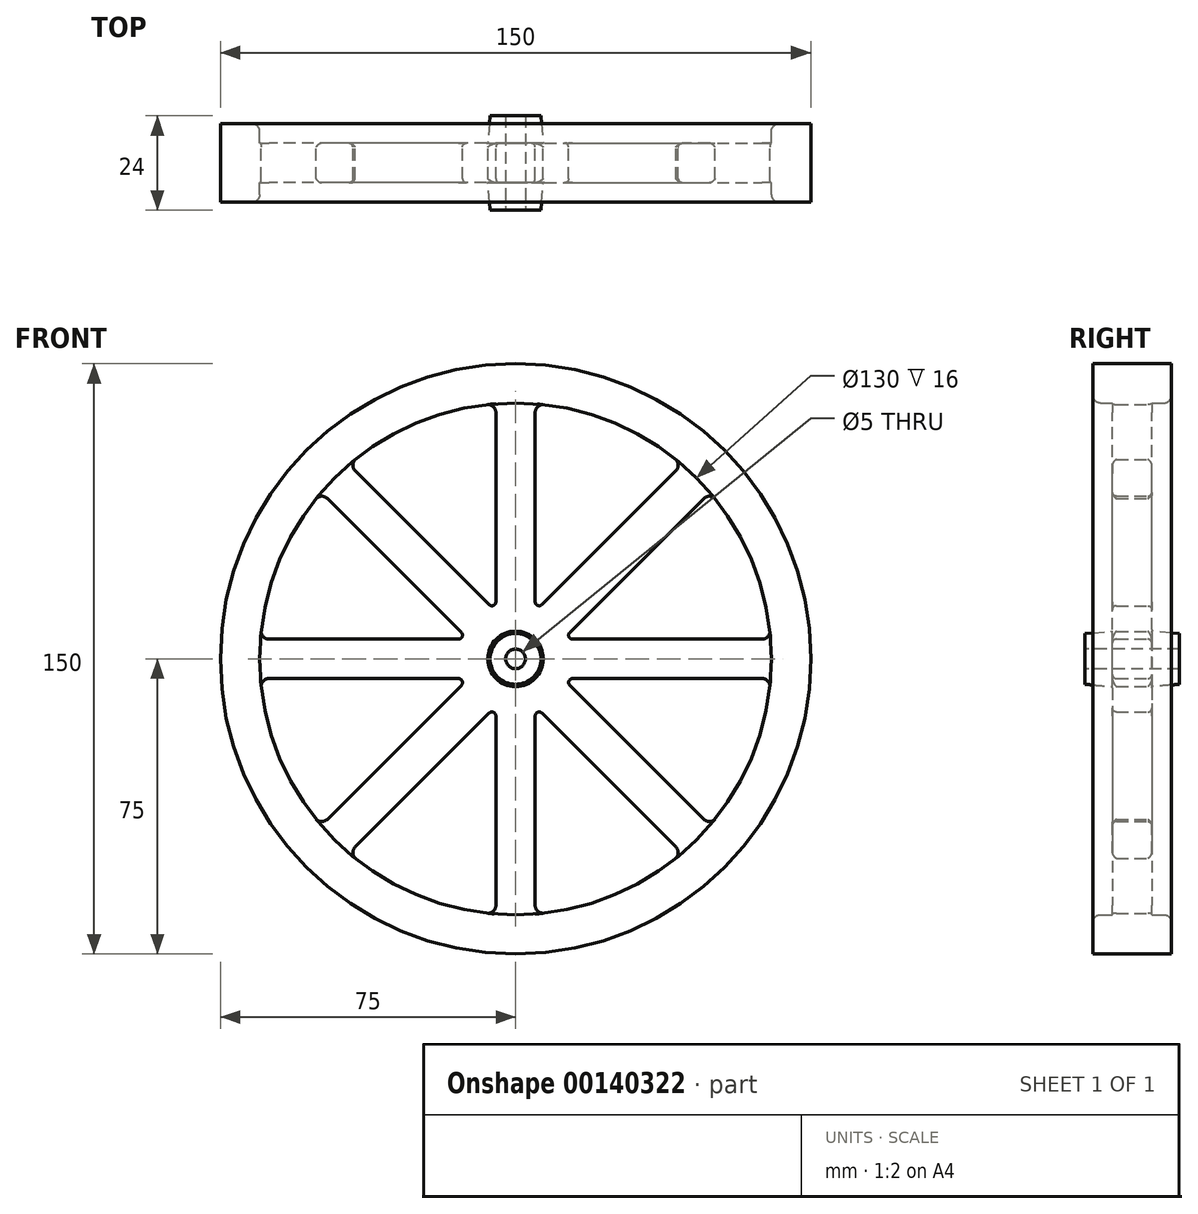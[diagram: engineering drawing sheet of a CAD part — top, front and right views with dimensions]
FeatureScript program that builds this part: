
annotation { "Feature Type Name" : "Feature", "Feature Type Description" : "" }
export const myFeature = defineFeature(function(context is Context, id is Id, definition is map)
    precondition{}
    {
        {
            var Q0;
            Q0=qCreatedBy(makeId("Front.planeOp"),FACE);
            var sketch = newSketch(context, id + "F0", { "sketchPlane" : qUnion([Q0])});
            skCircle(sketch, "E0", {"center": v(0, 0) * mm, "radius": 75 * mm});
            skLineSegment(sketch, "E1", {"start": v(0, 0) * mm, "end": v(-53.03, 53.03) * mm, "construction": true});
            skLineSegment(sketch, "E2", {"start": v(-6.7, 13.78) * mm, "end": v(-40.74, 47.82) * mm});
            skLineSegment(sketch, "E3", {"start": v(-5, 14.49) * mm, "end": v(-5, 62.62) * mm});
            skLineSegment(sketch, "E4", {"start": v(0, 0) * mm, "end": v(-5, 12.07) * mm, "construction": true});
            skCircle(sketch, "E5.1.7.0", {"center": v(0, 0) * mm, "radius": 65 * mm});
            skPoint(sketch, "E6.visualSharp", {"position": v(-14.87, 21.95) * mm});
            skArc(sketch, "E6.filletArc", {"start": v(-40.74, 50.64) * mm, "mid": v(-41.33, 49.23) * mm, "end": v(-40.74, 47.82) * mm});
            skPoint(sketch, "E7.visualSharp", {"position": v(-5, 26.04) * mm});
            skArc(sketch, "E7.filletArc", {"start": v(-5, 62.62) * mm, "mid": v(-5.59, 64.04) * mm, "end": v(-7, 64.62) * mm});
            skPoint(sketch, "E8.visualSharp", {"position": v(-5, 12.07) * mm});
            skArc(sketch, "E8.filletArc", {"start": v(-6.7, 13.78) * mm, "mid": v(-5.62, 13.56) * mm, "end": v(-5, 14.49) * mm});
            skArc(sketch, "E9.1.0", {"start": v(-64.62, 7) * mm, "mid": v(-64.04, 5.59) * mm, "end": v(-62.62, 5) * mm});
            skLineSegment(sketch, "E9.1.1", {"start": v(-14.49, 5) * mm, "end": v(-62.62, 5) * mm});
            skArc(sketch, "E9.1.2", {"start": v(-14.49, 5) * mm, "mid": v(-13.56, 5.62) * mm, "end": v(-13.78, 6.7) * mm});
            skLineSegment(sketch, "E9.1.3", {"start": v(-13.78, 6.7) * mm, "end": v(-47.82, 40.74) * mm});
            skArc(sketch, "E9.1.4", {"start": v(-47.82, 40.74) * mm, "mid": v(-49.23, 41.33) * mm, "end": v(-50.64, 40.74) * mm});
            skArc(sketch, "E9.2.0", {"start": v(-50.64, -40.74) * mm, "mid": v(-49.23, -41.33) * mm, "end": v(-47.82, -40.74) * mm});
            skLineSegment(sketch, "E9.2.1", {"start": v(-13.78, -6.7) * mm, "end": v(-47.82, -40.74) * mm});
            skArc(sketch, "E9.2.2", {"start": v(-13.78, -6.7) * mm, "mid": v(-13.56, -5.62) * mm, "end": v(-14.49, -5) * mm});
            skLineSegment(sketch, "E9.2.3", {"start": v(-14.49, -5) * mm, "end": v(-62.62, -5) * mm});
            skArc(sketch, "E9.2.4", {"start": v(-62.62, -5) * mm, "mid": v(-64.04, -5.59) * mm, "end": v(-64.62, -7) * mm});
            skArc(sketch, "E9.3.0", {"start": v(-7, -64.62) * mm, "mid": v(-5.59, -64.04) * mm, "end": v(-5, -62.62) * mm});
            skLineSegment(sketch, "E9.3.1", {"start": v(-5, -14.49) * mm, "end": v(-5, -62.62) * mm});
            skArc(sketch, "E9.3.2", {"start": v(-5, -14.49) * mm, "mid": v(-5.62, -13.56) * mm, "end": v(-6.7, -13.78) * mm});
            skLineSegment(sketch, "E9.3.3", {"start": v(-6.7, -13.78) * mm, "end": v(-40.74, -47.82) * mm});
            skArc(sketch, "E9.3.4", {"start": v(-40.74, -47.82) * mm, "mid": v(-41.33, -49.23) * mm, "end": v(-40.74, -50.64) * mm});
            skArc(sketch, "E9.4.0", {"start": v(40.74, -50.64) * mm, "mid": v(41.33, -49.23) * mm, "end": v(40.74, -47.82) * mm});
            skLineSegment(sketch, "E9.4.1", {"start": v(6.7, -13.78) * mm, "end": v(40.74, -47.82) * mm});
            skArc(sketch, "E9.4.2", {"start": v(6.7, -13.78) * mm, "mid": v(5.62, -13.56) * mm, "end": v(5, -14.49) * mm});
            skLineSegment(sketch, "E9.4.3", {"start": v(5, -14.49) * mm, "end": v(5, -62.62) * mm});
            skArc(sketch, "E9.4.4", {"start": v(5, -62.62) * mm, "mid": v(5.59, -64.04) * mm, "end": v(7, -64.62) * mm});
            skArc(sketch, "E9.5.0", {"start": v(64.62, -7) * mm, "mid": v(64.04, -5.59) * mm, "end": v(62.62, -5) * mm});
            skLineSegment(sketch, "E9.5.1", {"start": v(14.49, -5) * mm, "end": v(62.62, -5) * mm});
            skArc(sketch, "E9.5.2", {"start": v(14.49, -5) * mm, "mid": v(13.56, -5.62) * mm, "end": v(13.78, -6.7) * mm});
            skLineSegment(sketch, "E9.5.3", {"start": v(13.78, -6.7) * mm, "end": v(47.82, -40.74) * mm});
            skArc(sketch, "E9.5.4", {"start": v(47.82, -40.74) * mm, "mid": v(49.23, -41.33) * mm, "end": v(50.64, -40.74) * mm});
            skArc(sketch, "E9.6.0", {"start": v(50.64, 40.74) * mm, "mid": v(49.23, 41.33) * mm, "end": v(47.82, 40.74) * mm});
            skLineSegment(sketch, "E9.6.1", {"start": v(13.78, 6.7) * mm, "end": v(47.82, 40.74) * mm});
            skArc(sketch, "E9.6.2", {"start": v(13.78, 6.7) * mm, "mid": v(13.56, 5.62) * mm, "end": v(14.49, 5) * mm});
            skLineSegment(sketch, "E9.6.3", {"start": v(14.49, 5) * mm, "end": v(62.62, 5) * mm});
            skArc(sketch, "E9.6.4", {"start": v(62.62, 5) * mm, "mid": v(64.04, 5.59) * mm, "end": v(64.62, 7) * mm});
            skArc(sketch, "E9.7.0", {"start": v(7, 64.62) * mm, "mid": v(5.59, 64.04) * mm, "end": v(5, 62.62) * mm});
            skLineSegment(sketch, "E9.7.1", {"start": v(5, 14.49) * mm, "end": v(5, 62.62) * mm});
            skArc(sketch, "E9.7.2", {"start": v(5, 14.49) * mm, "mid": v(5.62, 13.56) * mm, "end": v(6.7, 13.78) * mm});
            skLineSegment(sketch, "E9.7.3", {"start": v(6.7, 13.78) * mm, "end": v(40.74, 47.82) * mm});
            skArc(sketch, "E9.7.4", {"start": v(40.74, 47.82) * mm, "mid": v(41.33, 49.23) * mm, "end": v(40.74, 50.64) * mm});
            skCircle(sketch, "E10", {"center": v(0, 0) * mm, "radius": 2.5 * mm});
            skCircle(sketch, "E11", {"center": v(0, 0) * mm, "radius": 7.5 * mm});
            skLineSegment(sketch, "E12", {"start": v(6.7, 13.78) * mm, "end": v(5, 12.07) * mm, "construction": true});
            skLineSegment(sketch, "E13", {"start": v(5, 14.49) * mm, "end": v(5, 12.07) * mm, "construction": true});
            skSolve(sketch);
        }
        {
            var Q0;
            Q0=makeQuery(id+"F0.imprint","IMPRINT",FACE,{"disambiguationData":[TD([[makeQuery(id+"F0.imprint","IMPRINT",EDGE,{"derivedFrom":sQuery(id+"F0.wireOp",EDGE,"E0")}),1.0]])]});
            extrude(context, id + "F1", {"entities" : qUnion([Q0]), "endBound" : BoundingType.SYMMETRIC, "depth" : 20 * mm});
        }
        {
            var Q0;
            Q0=makeQuery(id+"F0.imprint","IMPRINT",FACE,{"disambiguationData":[TD([[makeQuery(id+"F0.imprint","IMPRINT",EDGE,{"derivedFrom":sQuery(id+"F0.wireOp",EDGE,"E2")}),1.0]])]});
            var Q1;
            Q1=makeQuery(id+"F0.imprint","IMPRINT",FACE,{"disambiguationData":[TD([[makeQuery(id+"F0.imprint","IMPRINT",EDGE,{"derivedFrom":sQuery(id+"F0.wireOp",EDGE,"E10")}),-1.0]])]});
            extrude(context, id + "F2", {"entities" : qUnion([Q0, Q1]), "operationType" : NewBodyOperationType.ADD, "endBound" : BoundingType.SYMMETRIC, "depth" : 10 * mm});
        }
        {
            var Q0;
            Q0=makeQuery(id+"F0.imprint","IMPRINT",FACE,{"disambiguationData":[TD([[makeQuery(id+"F0.imprint","IMPRINT",EDGE,{"derivedFrom":sQuery(id+"F0.wireOp",EDGE,"E10")}),-1.0]])]});
            var Q1;
            Q1=makeQuery(id+"F0.imprint","IMPRINT",FACE,{"disambiguationData":[TD([[makeQuery(id+"F0.imprint","IMPRINT",EDGE,{"derivedFrom":sQuery(id+"F0.wireOp",EDGE,"E10")}),1.0]])]});
            extrude(context, id + "F3", {"entities" : qUnion([Q0, Q1]), "operationType" : NewBodyOperationType.ADD, "endBound" : BoundingType.SYMMETRIC, "depth" : 24 * mm, "hasDraft" : true, "draftAngle" : 5 * degree, "draftPullDirection" : true});
        }
        {
            var Q0;
            Q0=makeQuery(id+"F0.imprint","IMPRINT",FACE,{"disambiguationData":[TD([[makeQuery(id+"F0.imprint","IMPRINT",EDGE,{"derivedFrom":sQuery(id+"F0.wireOp",EDGE,"E10")}),1.0]])]});
            extrude(context, id + "F4", {"entities" : qUnion([Q0]), "operationType" : NewBodyOperationType.REMOVE, "endBound" : BoundingType.SYMMETRIC, "oppositeDirection" : true, "depth" : 25 * mm});
        }
        {
            var Q0;
            Q0=makeQuery(id+"F1.opExtrude","CAP_EDGE",EDGE,{"disambiguationData":[OSD([sQuery(id+"F0.wireOp",EDGE,"E5.1.7.0")])],"isStart":true});
            var Q1;
            Q1=makeQuery(id+"F1.opExtrude","CAP_EDGE",EDGE,{"disambiguationData":[OSD([sQuery(id+"F0.wireOp",EDGE,"E5.1.7.0")])],"isStart":false});
            fillet(context, id + "F5", {"entities" : qUnion([Q0, Q1]), "radius" : 2 * mm, "tangentPropagation" : true, "allowEdgeOverflow" : false});
        }
        {
            var Q0;
            Q0=makeQuery(id+"F2.opExtrude","CAP_EDGE",EDGE,{"disambiguationData":[OSD([sQuery(id+"F0.wireOp",EDGE,"E9.1.3")])],"isStart":false});
            var Q1;
            Q1=makeQuery(id+"F2.opExtrude","CAP_EDGE",EDGE,{"disambiguationData":[OSD([sQuery(id+"F0.wireOp",EDGE,"E9.2.3")])],"isStart":false});
            var Q2;
            Q2=makeQuery(id+"F2.opExtrude","CAP_EDGE",EDGE,{"disambiguationData":[OSD([sQuery(id+"F0.wireOp",EDGE,"E9.3.3")])],"isStart":false});
            var Q3;
            Q3=makeQuery(id+"F2.opExtrude","CAP_EDGE",EDGE,{"disambiguationData":[OSD([sQuery(id+"F0.wireOp",EDGE,"E9.4.3")])],"isStart":false});
            var Q4;
            Q4=makeQuery(id+"F2.opExtrude","CAP_EDGE",EDGE,{"disambiguationData":[OSD([sQuery(id+"F0.wireOp",EDGE,"E9.5.3")])],"isStart":false});
            var Q5;
            Q5=makeQuery(id+"F2.opExtrude","CAP_EDGE",EDGE,{"disambiguationData":[OSD([sQuery(id+"F0.wireOp",EDGE,"E9.6.3")])],"isStart":false});
            var Q6;
            Q6=makeQuery(id+"F2.opExtrude","CAP_EDGE",EDGE,{"disambiguationData":[OSD([sQuery(id+"F0.wireOp",EDGE,"E9.7.3")])],"isStart":false});
            var Q7;
            Q7=makeQuery(id+"F2.opExtrude","CAP_EDGE",EDGE,{"disambiguationData":[OSD([sQuery(id+"F0.wireOp",EDGE,"E3")])],"isStart":false});
            var Q8;
            Q8=makeQuery(id+"F2.opExtrude","CAP_EDGE",EDGE,{"disambiguationData":[OSD([sQuery(id+"F0.wireOp",EDGE,"E9.2.3")])],"isStart":true});
            var Q9;
            Q9=makeQuery(id+"F2.opExtrude","CAP_EDGE",EDGE,{"disambiguationData":[OSD([sQuery(id+"F0.wireOp",EDGE,"E9.3.3")])],"isStart":true});
            var Q10;
            Q10=makeQuery(id+"F2.opExtrude","CAP_EDGE",EDGE,{"disambiguationData":[OSD([sQuery(id+"F0.wireOp",EDGE,"E3")])],"isStart":true});
            var Q11;
            Q11=makeQuery(id+"F2.opExtrude","CAP_EDGE",EDGE,{"disambiguationData":[OSD([sQuery(id+"F0.wireOp",EDGE,"E9.7.3")])],"isStart":true});
            var Q12;
            Q12=makeQuery(id+"F2.opExtrude","CAP_EDGE",EDGE,{"disambiguationData":[OSD([sQuery(id+"F0.wireOp",EDGE,"E9.6.3")])],"isStart":true});
            var Q13;
            Q13=makeQuery(id+"F2.opExtrude","CAP_EDGE",EDGE,{"disambiguationData":[OSD([sQuery(id+"F0.wireOp",EDGE,"E9.1.3")])],"isStart":true});
            var Q14;
            Q14=makeQuery(id+"F2.opExtrude","CAP_EDGE",EDGE,{"disambiguationData":[OSD([sQuery(id+"F0.wireOp",EDGE,"E9.4.3")])],"isStart":true});
            fillet(context, id + "F6", {"entities" : qUnion([Q0, Q1, Q2, Q3, Q4, Q5, Q6, Q7, Q8, Q9, Q10, Q11, Q12, Q13, Q14]), "radius" : 1 * mm, "tangentPropagation" : true, "allowEdgeOverflow" : false});
        }
    });
